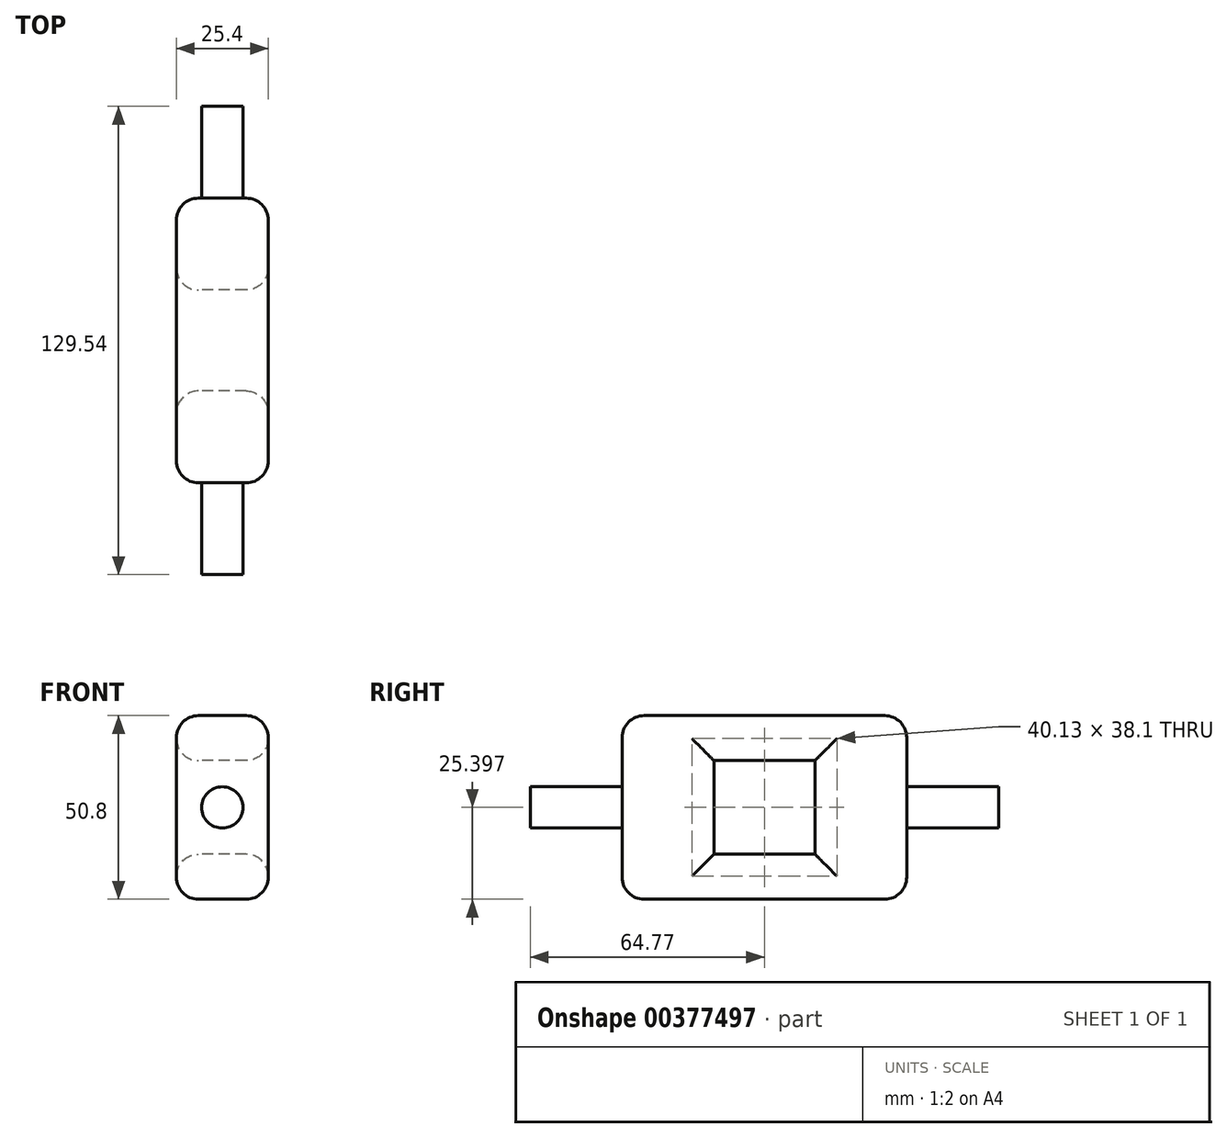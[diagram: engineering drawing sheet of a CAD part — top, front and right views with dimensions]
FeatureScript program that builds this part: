
annotation { "Feature Type Name" : "Feature", "Feature Type Description" : "" }
export const myFeature = defineFeature(function(context is Context, id is Id, definition is map)
    precondition{}
    {
        {
            var Q0;
            Q0=qCreatedBy(makeId("Front.planeOp"),FACE);
            var sketch = newSketch(context, id + "F0", { "sketchPlane" : qUnion([Q0])});
            skLineSegment(sketch, "E0", {"start": v(0, -49) * mm, "end": v(-12.7, -49) * mm});
            skLineSegment(sketch, "E1", {"start": v(-12.7, -49) * mm, "end": v(-12.7, 1.8) * mm});
            skLineSegment(sketch, "E2.MirrorCS", {"start": v(0, -49) * mm, "end": v(12.7, -49) * mm});
            skLineSegment(sketch, "E3.MirrorCS", {"start": v(12.7, -49) * mm, "end": v(12.7, 1.8) * mm});
            skLineSegment(sketch, "E4", {"start": v(12.7, 1.8) * mm, "end": v(-12.7, 1.8) * mm});
            skSolve(sketch);
        }
        {
            var Q0;
            Q0 = qSketchRegion(id + "F0", true);
            extrude(context, id + "F1", {"entities" : qUnion([Q0]), "depth" : 25.4 * mm});
        }
        {
            var Q0;
            Q0=makeQuery(id+"F1.opExtrude","SWEPT_FACE",FACE,{"disambiguationData":[OSD([sQuery(id+"F0.wireOp",EDGE,"E1")])]});
            var sketch = newSketch(context, id + "F2", { "sketchPlane" : qUnion([Q0])});
            skLineSegment(sketch, "E5", {"start": v(0, -10.65) * mm, "end": v(53.34, -10.65) * mm});
            skLineSegment(sketch, "E6", {"start": v(0, -36.56) * mm, "end": v(53.34, -36.56) * mm});
            skLineSegment(sketch, "E7", {"start": v(25.4, 1.8) * mm, "end": v(53.34, 1.8) * mm});
            skLineSegment(sketch, "E8", {"start": v(25.4, -49) * mm, "end": v(53.34, -49) * mm});
            skLineSegment(sketch, "E9", {"start": v(53.34, 1.8) * mm, "end": v(53.34, -10.65) * mm});
            skLineSegment(sketch, "E10", {"start": v(53.34, -36.56) * mm, "end": v(53.34, -49) * mm});
            skSolve(sketch);
        }
        {
            var Q0;
            Q0 = qSketchRegion(id + "F2", true);
            var Q1;
            {var subQ5=sQuery(id+"F2.wireOp",EDGE,"E7");Q1=makeQuery(id+"F2.imprint","IMPRINT",FACE,{"disambiguationData":[TD([[makeQuery(id+"F2.imprint","IMPRINT",EDGE,{"derivedFrom":subQ5}),-1.0]])]});}
            var Q2;
            {var subQ5=sQuery(id+"F2.wireOp",EDGE,"E8");Q2=makeQuery(id+"F2.imprint","IMPRINT",FACE,{"disambiguationData":[TD([[makeQuery(id+"F2.imprint","IMPRINT",EDGE,{"derivedFrom":subQ5}),1.0]])]});}
            extrude(context, id + "F3", {"entities" : qUnion([Q0, Q1, Q2]), "operationType" : NewBodyOperationType.ADD, "depth" : -25.4 * mm});
        }
        {
            var Q0;
            Q0=makeQuery(id+"F1.opExtrude","CAP_FACE",FACE,{"disambiguationData":[OSD([sQuery(id+"F0.wireOp",EDGE,"E0"),sQuery(id+"F0.wireOp",EDGE,"E1"),sQuery(id+"F0.wireOp",EDGE,"E2.MirrorCS"),sQuery(id+"F0.wireOp",EDGE,"E3.MirrorCS"),sQuery(id+"F0.wireOp",EDGE,"E4")])],"isStart":true});
            var sketch = newSketch(context, id + "F4", { "sketchPlane" : qUnion([Q0])});
            skLineSegment(sketch, "E11", {"start": v(12.7, -23.6) * mm, "end": v(0, -23.6) * mm});
            skCircle(sketch, "E12", {"center": v(0, -23.6) * mm, "radius": 5.72 * mm});
            skSolve(sketch);
        }
        {
            var Q0;
            Q0 = qSketchRegion(id + "F4", true);
            extrude(context, id + "F5", {"entities" : qUnion([Q0]), "operationType" : NewBodyOperationType.ADD, "depth" : 25.4 * mm});
        }
        {
            var Q0;
            Q0=makeQuery(id+"F3.opExtrude","SWEPT_FACE",FACE,{"disambiguationData":[OSD([sQuery(id+"F2.wireOp",EDGE,"E9")])]});
            var sketch = newSketch(context, id + "F6", { "sketchPlane" : qUnion([Q0])});
            skPoint(sketch, "E13.startSnap0", {"position": v(-12.7, -4.55) * mm});
            skLineSegment(sketch, "E14", {"start": v(-12.7, 1.8) * mm, "end": v(12.7, 1.8) * mm});
            skLineSegment(sketch, "E15", {"start": v(12.7, 1.8) * mm, "end": v(12.7, -49) * mm});
            skLineSegment(sketch, "E16", {"start": v(12.7, -49) * mm, "end": v(-12.7, -49) * mm});
            skLineSegment(sketch, "E17", {"start": v(-12.7, -49) * mm, "end": v(-12.7, 1.8) * mm});
            skSolve(sketch);
        }
        {
            var Q0;
            Q0 = qSketchRegion(id + "F6", true);
            extrude(context, id + "F7", {"entities" : qUnion([Q0]), "operationType" : NewBodyOperationType.ADD, "depth" : 25.4 * mm});
        }
        {
            var Q0;
            Q0=makeQuery(id+"F1.opExtrude","CAP_EDGE",EDGE,{"disambiguationData":[OSD([sQuery(id+"F0.wireOp",EDGE,"E1")])],"isStart":true});
            var Q1;
            Q1=makeQuery(id+"F1.opExtrude","CAP_EDGE",EDGE,{"disambiguationData":[OSD([sQuery(id+"F0.wireOp",EDGE,"E3.MirrorCS")])],"isStart":true});
            var Q2;
            Q2=makeQuery(id+"F1.opExtrude","CAP_EDGE",EDGE,{"disambiguationData":[OSD([sQuery(id+"F0.wireOp",EDGE,"E4")])],"isStart":true});
            var Q3;
            Q3=makeQuery(id+"F1.opExtrude","CAP_EDGE",EDGE,{"disambiguationData":[OSD([sQuery(id+"F0.wireOp",EDGE,"E0"),sQuery(id+"F0.wireOp",EDGE,"E2.MirrorCS")])],"isStart":true});
            var Q4;
            Q4=makeQuery(id+"F3.opExtrude","CAP_EDGE",EDGE,{"disambiguationData":[OSD([sQuery(id+"F2.wireOp",EDGE,"E6")])],"isStart":true});
            var Q5;
            Q5=makeQuery(id+"F3.opExtrude","CAP_EDGE",EDGE,{"disambiguationData":[OSD([sQuery(id+"F2.wireOp",EDGE,"E5")])],"isStart":true});
            var Q6;
            Q6=makeQuery(id+"F3.opExtrude","CAP_EDGE",EDGE,{"disambiguationData":[OSD([sQuery(id+"F2.wireOp",EDGE,"E6")])],"isStart":false});
            var Q7;
            Q7=makeQuery(id+"F3.opExtrude","CAP_EDGE",EDGE,{"disambiguationData":[OSD([sQuery(id+"F2.wireOp",EDGE,"E5")])],"isStart":false});
            var Q8;
            Q8=makeQuery(id+"F3.boolean.opBoolean","MERGE",EDGE,{"derivedFrom":[makeQuery(id+"F1.opExtrude","SWEPT_EDGE",EDGE,{"disambiguationData":[OSD([sQuery(id+"F0.wireOp",EDGE,"E1"),sQuery(id+"F0.wireOp",EDGE,"E4")])]}),makeQuery(id+"F3.opExtrude","CAP_EDGE",EDGE,{"disambiguationData":[OSD([sQuery(id+"F2.wireOp",EDGE,"E7")])],"isStart":true})]});
            var Q9;
            Q9=makeQuery(id+"F3.boolean.opBoolean","MERGE",EDGE,{"derivedFrom":[makeQuery(id+"F1.opExtrude","SWEPT_EDGE",EDGE,{"disambiguationData":[OSD([sQuery(id+"F0.wireOp",EDGE,"E3.MirrorCS"),sQuery(id+"F0.wireOp",EDGE,"E4")])]}),makeQuery(id+"F3.opExtrude","CAP_EDGE",EDGE,{"disambiguationData":[OSD([sQuery(id+"F2.wireOp",EDGE,"E7")])],"isStart":false})]});
            var Q10;
            Q10=makeQuery(id+"F3.boolean.opBoolean","MERGE",EDGE,{"derivedFrom":[makeQuery(id+"F1.opExtrude","SWEPT_EDGE",EDGE,{"disambiguationData":[OSD([sQuery(id+"F0.wireOp",EDGE,"E2.MirrorCS"),sQuery(id+"F0.wireOp",EDGE,"E3.MirrorCS")])]}),makeQuery(id+"F3.opExtrude","CAP_EDGE",EDGE,{"disambiguationData":[OSD([sQuery(id+"F2.wireOp",EDGE,"E8")])],"isStart":false})]});
            var Q11;
            Q11=makeQuery(id+"F3.boolean.opBoolean","MERGE",EDGE,{"derivedFrom":[makeQuery(id+"F1.opExtrude","SWEPT_EDGE",EDGE,{"disambiguationData":[OSD([sQuery(id+"F0.wireOp",EDGE,"E0"),sQuery(id+"F0.wireOp",EDGE,"E1")])]}),makeQuery(id+"F3.opExtrude","CAP_EDGE",EDGE,{"disambiguationData":[OSD([sQuery(id+"F2.wireOp",EDGE,"E8")])],"isStart":true})]});
            var Q12;
            Q12=makeQuery(id+"F1.opExtrude","CAP_EDGE",EDGE,{"disambiguationData":[OSD([sQuery(id+"F0.wireOp",EDGE,"E1")])],"isStart":false});
            var Q13;
            Q13=makeQuery(id+"F1.opExtrude","CAP_EDGE",EDGE,{"disambiguationData":[OSD([sQuery(id+"F0.wireOp",EDGE,"E3.MirrorCS")])],"isStart":false});
            var Q14;
            Q14=makeQuery(id+"F7.opExtrude","CAP_EDGE",EDGE,{"disambiguationData":[OSD([sQuery(id+"F6.wireOp",EDGE,"E14")])],"isStart":false});
            var Q15;
            Q15=makeQuery(id+"F7.opExtrude","CAP_EDGE",EDGE,{"disambiguationData":[OSD([sQuery(id+"F6.wireOp",EDGE,"E16")])],"isStart":false});
            var Q16;
            Q16=makeQuery(id+"F7.opExtrude","CAP_EDGE",EDGE,{"disambiguationData":[OSD([sQuery(id+"F6.wireOp",EDGE,"E17")])],"isStart":false});
            var Q17;
            Q17=makeQuery(id+"F7.opExtrude","CAP_EDGE",EDGE,{"disambiguationData":[OSD([sQuery(id+"F6.wireOp",EDGE,"E15")])],"isStart":false});
            var Q18;
            Q18=makeQuery(id+"F7.opExtrude","CAP_EDGE",EDGE,{"disambiguationData":[OSD([sQuery(id+"F6.wireOp",EDGE,"E17")])],"isStart":true});
            var Q19;
            Q19=makeQuery(id+"F7.opExtrude","CAP_EDGE",EDGE,{"disambiguationData":[OSD([sQuery(id+"F6.wireOp",EDGE,"E15")])],"isStart":true});
            fillet(context, id + "F8", {"entities" : qUnion([Q0, Q1, Q2, Q3, Q4, Q5, Q6, Q7, Q8, Q9, Q10, Q11, Q12, Q13, Q14, Q15, Q16, Q17, Q18, Q19]), "radius" : 6.1 * mm, "tangentPropagation" : true, "allowEdgeOverflow" : false});
        }
        {
            var Q0;
            Q0=makeQuery(id+"F7.opExtrude","CAP_FACE",FACE,{"disambiguationData":[OSD([sQuery(id+"F6.wireOp",EDGE,"E14"),sQuery(id+"F6.wireOp",EDGE,"E15"),sQuery(id+"F6.wireOp",EDGE,"E16"),sQuery(id+"F6.wireOp",EDGE,"E17")])],"isStart":false});
            var sketch = newSketch(context, id + "F9", { "sketchPlane" : qUnion([Q0])});
            skLineSegment(sketch, "E18", {"start": v(0, -4.3) * mm, "end": v(0, -42.9) * mm});
            skLineSegment(sketch, "E19", {"start": v(0, -42.9) * mm, "end": v(0, -23.6) * mm});
            skCircle(sketch, "E20", {"center": v(0, -23.6) * mm, "radius": 5.72 * mm});
            skSolve(sketch);
        }
        {
            var Q0;
            Q0 = qSketchRegion(id + "F9", true);
            extrude(context, id + "F10", {"entities" : qUnion([Q0]), "operationType" : NewBodyOperationType.ADD, "depth" : 25.4 * mm});
        }
    });
